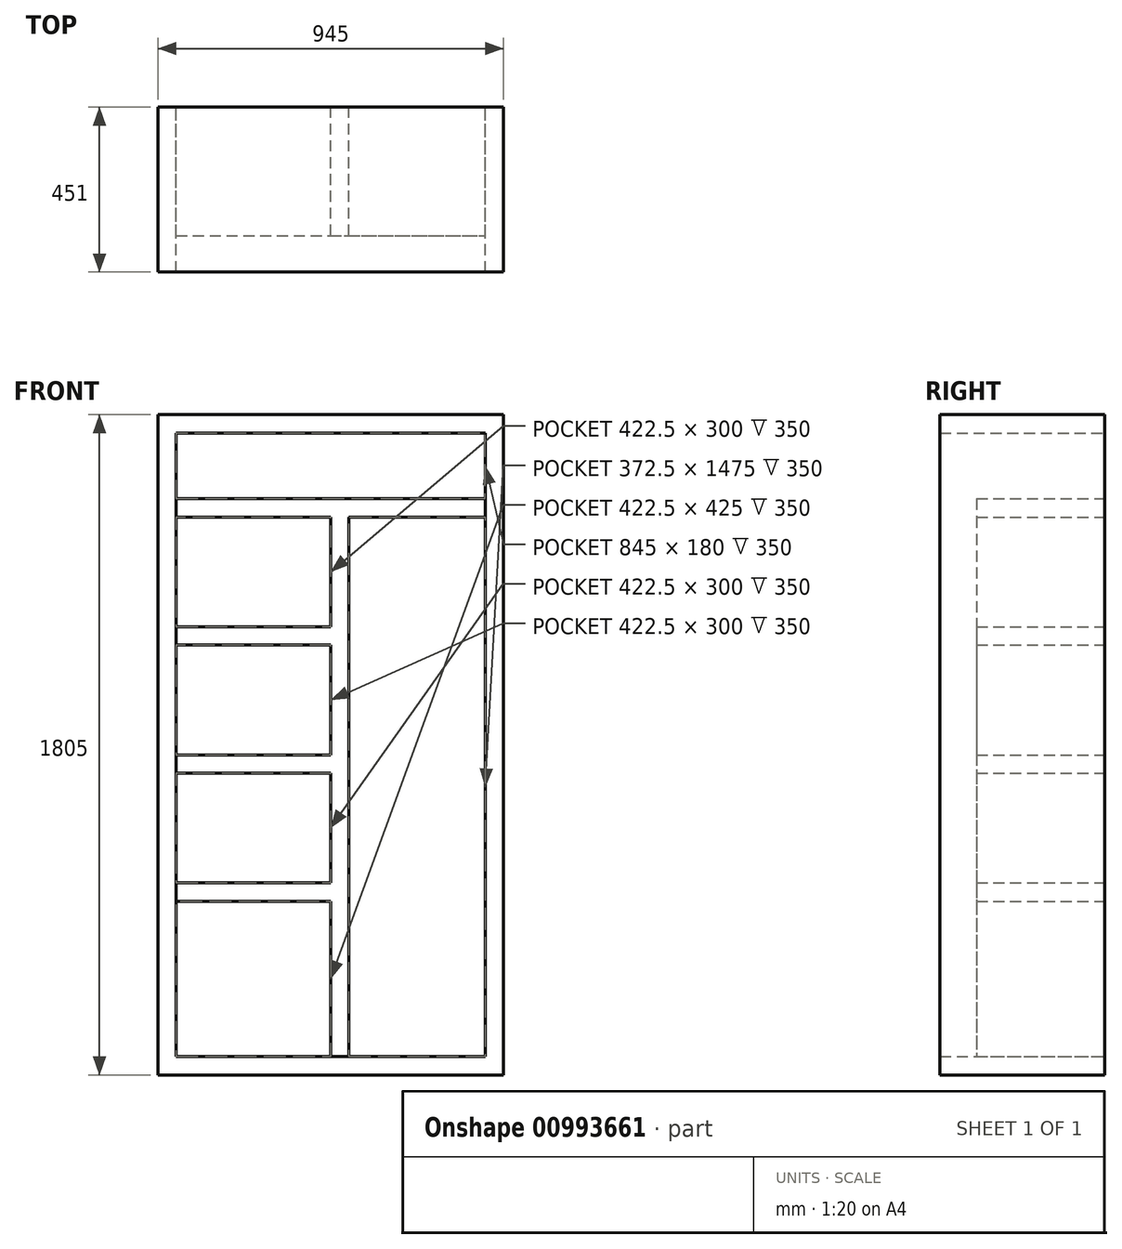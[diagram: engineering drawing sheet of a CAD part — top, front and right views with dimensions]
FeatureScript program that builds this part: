
annotation { "Feature Type Name" : "Feature", "Feature Type Description" : "" }
export const myFeature = defineFeature(function(context is Context, id is Id, definition is map)
    precondition{}
    {
        {
            var Q0;
            Q0=qCreatedBy(makeId("Front.planeOp"),FACE);
            var sketch = newSketch(context, id + "F0", { "sketchPlane" : qUnion([Q0])});
            skLineSegment(sketch, "E0.bottom", {"start": v(-472.5, 902.5) * mm, "end": v(472.5, 902.5) * mm});
            skLineSegment(sketch, "E0.top", {"start": v(-472.5, -902.5) * mm, "end": v(472.5, -902.5) * mm});
            skLineSegment(sketch, "E0.left", {"start": v(-472.5, 902.5) * mm, "end": v(-472.5, -902.5) * mm});
            skLineSegment(sketch, "E0.right", {"start": v(472.5, 902.5) * mm, "end": v(472.5, -902.5) * mm});
            skLineSegment(sketch, "E1", {"start": v(-915.42, 0) * mm, "end": v(898.2, 0) * mm, "construction": true});
            skLineSegment(sketch, "E2", {"start": v(0, 1036.04) * mm, "end": v(0, -1074.82) * mm, "construction": true});
            skLineSegment(sketch, "E3.0", {"start": v(-422.5, 852.5) * mm, "end": v(422.5, 852.5) * mm});
            skLineSegment(sketch, "E3.1", {"start": v(-422.5, 852.5) * mm, "end": v(-422.5, -852.5) * mm});
            skLineSegment(sketch, "E3.2", {"start": v(-422.5, -852.5) * mm, "end": v(422.5, -852.5) * mm});
            skLineSegment(sketch, "E3.3", {"start": v(422.5, 852.5) * mm, "end": v(422.5, -852.5) * mm});
            skSolve(sketch);
        }
        {
            var Q0;
            Q0 = qSketchRegion(id + "F0", true);
            extrude(context, id + "F1", {"entities" : qUnion([Q0]), "depth" : 450 * mm, "offsetDistance" : 25.4 * mm});
        }
        {
            var Q0;
            Q0=makeQuery(id+"F1.opExtrude","CAP_FACE",FACE,{"disambiguationData":[OSD([sQuery(id+"F0.wireOp",EDGE,"E0.bottom"),sQuery(id+"F0.wireOp",EDGE,"E0.top"),sQuery(id+"F0.wireOp",EDGE,"E0.left"),sQuery(id+"F0.wireOp",EDGE,"E0.right"),sQuery(id+"F0.wireOp",EDGE,"E3.0"),sQuery(id+"F0.wireOp",EDGE,"E3.1"),sQuery(id+"F0.wireOp",EDGE,"E3.2"),sQuery(id+"F0.wireOp",EDGE,"E3.3")])],"isStart":true});
            var sketch = newSketch(context, id + "F2", { "sketchPlane" : qUnion([Q0])});
            skLineSegment(sketch, "E4.bottom", {"start": v(-472.5, 902.5) * mm, "end": v(472.5, 902.5) * mm});
            skLineSegment(sketch, "E4.top", {"start": v(-472.5, -902.5) * mm, "end": v(472.5, -902.5) * mm});
            skLineSegment(sketch, "E4.left", {"start": v(-472.5, 902.5) * mm, "end": v(-472.5, -902.5) * mm});
            skLineSegment(sketch, "E4.right", {"start": v(472.5, 902.5) * mm, "end": v(472.5, -902.5) * mm});
            skSolve(sketch);
        }
        {
            var Q0;
            Q0 = qSketchRegion(id + "F2", true);
            extrude(context, id + "F3", {"entities" : qUnion([Q0]), "operationType" : NewBodyOperationType.ADD, "depth" : 1 * mm, "offsetDistance" : 25.4 * mm});
        }
        {
            var Q0;
            Q0=makeQuery(id+"F3.opExtrude","CAP_FACE",FACE,{"disambiguationData":[OSD([sQuery(id+"F2.wireOp",EDGE,"E4.bottom"),sQuery(id+"F2.wireOp",EDGE,"E4.top"),sQuery(id+"F2.wireOp",EDGE,"E4.left"),sQuery(id+"F2.wireOp",EDGE,"E4.right")])],"isStart":true});
            var sketch = newSketch(context, id + "F4", { "sketchPlane" : qUnion([Q0])});
            skLineSegment(sketch, "E5.bottom", {"start": v(-422.5, 672.5) * mm, "end": v(422.5, 672.5) * mm});
            skLineSegment(sketch, "E5.top", {"start": v(-422.5, 622.5) * mm, "end": v(422.5, 622.5) * mm});
            skLineSegment(sketch, "E5.left", {"start": v(-422.5, 672.5) * mm, "end": v(-422.5, 622.5) * mm});
            skLineSegment(sketch, "E5.right", {"start": v(422.5, 672.5) * mm, "end": v(422.5, 622.5) * mm});
            skLineSegment(sketch, "E6.bottom", {"start": v(-422.5, 322.5) * mm, "end": v(0, 322.5) * mm});
            skLineSegment(sketch, "E6.top", {"start": v(-422.5, 272.5) * mm, "end": v(0, 272.5) * mm});
            skLineSegment(sketch, "E6.left", {"start": v(-422.5, 322.5) * mm, "end": v(-422.5, 272.5) * mm});
            skLineSegment(sketch, "E6.right", {"start": v(0, 322.5) * mm, "end": v(0, 272.5) * mm});
            skLineSegment(sketch, "E7.bottom", {"start": v(-422.5, -27.5) * mm, "end": v(0, -27.5) * mm});
            skLineSegment(sketch, "E7.top", {"start": v(-422.5, -77.5) * mm, "end": v(0, -77.5) * mm});
            skLineSegment(sketch, "E7.left", {"start": v(-422.5, -27.5) * mm, "end": v(-422.5, -77.5) * mm});
            skLineSegment(sketch, "E7.right", {"start": v(0, -27.5) * mm, "end": v(0, -77.5) * mm});
            skLineSegment(sketch, "E8.bottom", {"start": v(-422.5, -377.5) * mm, "end": v(0, -377.5) * mm});
            skLineSegment(sketch, "E8.top", {"start": v(-422.5, -427.5) * mm, "end": v(0, -427.5) * mm});
            skLineSegment(sketch, "E8.left", {"start": v(-422.5, -377.5) * mm, "end": v(-422.5, -427.5) * mm});
            skLineSegment(sketch, "E8.right", {"start": v(0, -377.5) * mm, "end": v(0, -427.5) * mm});
            skLineSegment(sketch, "E9.bottom", {"start": v(0, 622.5) * mm, "end": v(50, 622.5) * mm});
            skLineSegment(sketch, "E9.top", {"start": v(0, -852.5) * mm, "end": v(50, -852.5) * mm});
            skLineSegment(sketch, "E9.left", {"start": v(0, 622.5) * mm, "end": v(0, -852.5) * mm});
            skLineSegment(sketch, "E9.right", {"start": v(50, 622.5) * mm, "end": v(50, -852.5) * mm});
            skSolve(sketch);
        }
        {
            var Q0;
            Q0 = qSketchRegion(id + "F4", true);
            extrude(context, id + "F5", {"entities" : qUnion([Q0]), "operationType" : NewBodyOperationType.ADD, "depth" : 350 * mm, "offsetDistance" : 25.4 * mm});
        }
    });
